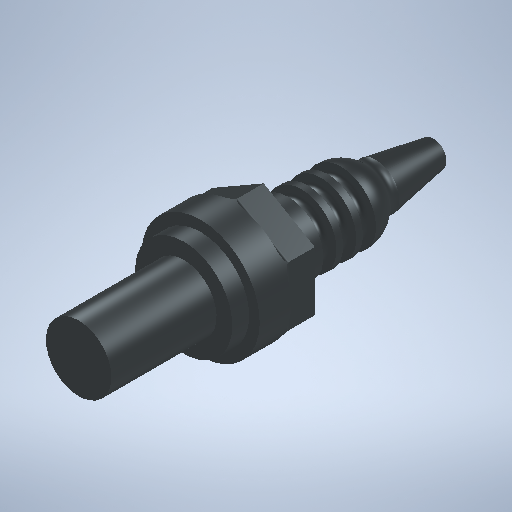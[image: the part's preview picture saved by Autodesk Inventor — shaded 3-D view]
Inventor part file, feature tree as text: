
AUTODESK INVENTOR PART (.ipt)
format: ipt  version: 2025 (Build 290162010, 162A)  size: 396,288 bytes
history: native  units: mm
features: sketch x4, plane x2, fillet x2, extrude x1, revolve x1, sweep x1
ambient origin geometry x8: Origin, YZ Plane, XZ Plane, XY Plane, X Axis, Y Axis, Z Axis, Center Point
bodies: Solid1 (feature_tree)
feature tree (11):
  extrude  "Extrusion1"  Depth=2.4mm TaperAngle=0.0deg
  plane  "Work Plane1"
  revolve  "Revolution1"  [1 undecoded]
  fillet  "Fillet1"  Radius=5.0mm
  fillet  "Fillet2"  Radius=7.4mm
  plane  "Work Plane2"
  sweep  "Sweep2"
  sketch  "Sketch1"  dims[d3=9.0mm d4=2.4mm d5=0.0mm]
  sketch  "Sketch2"  dims[d6=0.0mm d7=8.0mm d8=5.0mm d9=7.4mm]
  sketch  "Sketch3"  dims[d10=9.0mm d12=27.0mm]
  sketch  "Sketch4"  dims[d14=1.0mm d15=1.0mm d16=1.0mm d17=3.5mm d18=5.350991mm d19=0.5mm d20=0.5mm d21=2.4mm d22=90.0deg d23=0.45mm d24=0.45mm d25=4.5mm d26=0.5mm d27=2.0mm d28=1.0mm d31=0.35mm d32=0.0mm d33=0.0mm]
note: 1 required parameter value undecoded (feature->parameter linkage not recoverable at this tier; creation-order binding heuristic only, values carry confidence <= 0.55)
